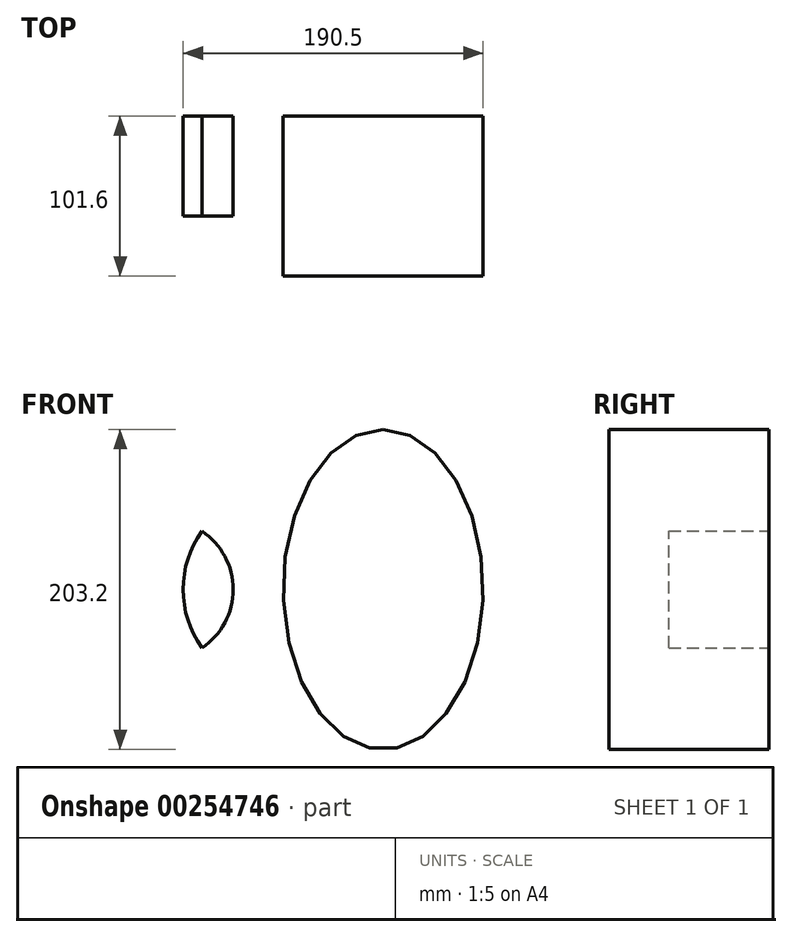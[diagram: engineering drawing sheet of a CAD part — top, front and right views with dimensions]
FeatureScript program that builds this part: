
annotation { "Feature Type Name" : "Feature", "Feature Type Description" : "" }
export const myFeature = defineFeature(function(context is Context, id is Id, definition is map)
    precondition{}
    {
        {
            var Q0;
            Q0=qCreatedBy(makeId("Front.planeOp"),FACE);
            var sketch = newSketch(context, id + "F0", { "sketchPlane" : qUnion([Q0])});
            skLineSegment(sketch, "E0", {"start": v(0, 0) * mm, "end": v(-76.2, 0) * mm});
            skCircle(sketch, "E1", {"center": v(-76.2, 0) * mm, "radius": 44.45 * mm});
            skLineSegment(sketch, "E2", {"start": v(-31.75, 0) * mm, "end": v(-63.5, 0) * mm});
            skCircle(sketch, "E3", {"center": v(0, 0) * mm, "radius": 63.5 * mm});
            skLineSegment(sketch, "E4", {"start": v(63.5, 0) * mm, "end": v(63.5, 101.6) * mm});
            skEllipse(sketch, "E5", {"center": v(63.5, 0) * mm, "majorRadius": 101.6 * mm, "minorRadius": 63.5 * mm, "majorAxis": v(0, 1)});
            skSolve(sketch);
        }
        {
            var Q0;
            {var subQ0=sQuery(id+"F0.wireOp",EDGE,"E3");var subQ1=sQuery(id+"F0.wireOp",EDGE,"E1");var subQ2=makeQuery(id+"F0.imprint","INTERSECT",VERTEX,{"disambiguationData":[OD(0.0)],"derivedFrom":[subQ1,subQ0]});Q0=makeQuery(id+"F0.imprint","IMPRINT",FACE,{"disambiguationData":[TD([[makeQuery(id+"F0.imprint","IMPRINT",EDGE,{"disambiguationData":[TD([[subQ2,-1.0]])],"derivedFrom":subQ1}),1.0]])]});}
            extrude(context, id + "F1", {"entities" : qUnion([Q0]), "depth" : 25.4 * mm});
        }
        {
            var Q0;
            {var subQ3=sQuery(id+"F0.wireOp",EDGE,"E1");var subQ5=sQuery(id+"F0.wireOp",EDGE,"E3");var subQ6=makeQuery(id+"F0.imprint","INTERSECT",VERTEX,{"disambiguationData":[OD(0.0)],"derivedFrom":[subQ3,subQ5]});Q0=makeQuery(id+"F0.imprint","IMPRINT",FACE,{"disambiguationData":[TD([[makeQuery(id+"F0.imprint","IMPRINT",EDGE,{"disambiguationData":[TD([[subQ6,1.0]])],"derivedFrom":subQ5}),1.0]])]});}
            var Q1;
            {var subQ0=sQuery(id+"F0.wireOp",EDGE,"E2");Q1=makeQuery(id+"F0.imprint","IMPRINT",FACE,{"disambiguationData":[TD([[makeQuery(id+"F0.imprint","IMPRINT",EDGE,{"derivedFrom":subQ0}),-1.0]])]});}
            var Q2;
            {var subQ0=sQuery(id+"F0.wireOp",EDGE,"E2");Q2=makeQuery(id+"F0.imprint","IMPRINT",FACE,{"disambiguationData":[TD([[makeQuery(id+"F0.imprint","IMPRINT",EDGE,{"derivedFrom":subQ0}),1.0]])]});}
            var Q3;
            {var subQ3=sQuery(id+"F0.wireOp",EDGE,"E1");var subQ5=sQuery(id+"F0.wireOp",EDGE,"E3");var subQ6=makeQuery(id+"F0.imprint","INTERSECT",VERTEX,{"disambiguationData":[OD(1.0)],"derivedFrom":[subQ3,subQ5]});Q3=makeQuery(id+"F0.imprint","IMPRINT",FACE,{"disambiguationData":[TD([[makeQuery(id+"F0.imprint","IMPRINT",EDGE,{"disambiguationData":[TD([[subQ6,-1.0]])],"derivedFrom":subQ5}),1.0]])]});}
            extrude(context, id + "F2", {"entities" : qUnion([Q0, Q1, Q2, Q3]), "operationType" : NewBodyOperationType.ADD, "depth" : 63.5 * mm});
        }
        {
            var Q0;
            {var subQ0=sQuery(id+"F0.wireOp",EDGE,"E4");Q0=makeQuery(id+"F0.imprint","IMPRINT",FACE,{"disambiguationData":[TD([[makeQuery(id+"F0.imprint","IMPRINT",EDGE,{"derivedFrom":subQ0}),1.0]])]});}
            var Q1;
            {var subQ0=sQuery(id+"F0.wireOp",EDGE,"E4");Q1=makeQuery(id+"F0.imprint","IMPRINT",FACE,{"disambiguationData":[TD([[makeQuery(id+"F0.imprint","IMPRINT",EDGE,{"derivedFrom":subQ0}),-1.0]])]});}
            var Q2;
            {var subQ0=sQuery(id+"F0.wireOp",EDGE,"E3");var subQ1=makeQuery(id+"F0.imprint","INTERSECT",VERTEX,{"derivedFrom":[subQ0,sQuery(id+"F0.wireOp",EDGE,"E4")]});Q2=makeQuery(id+"F0.imprint","IMPRINT",FACE,{"disambiguationData":[TD([[makeQuery(id+"F0.imprint","IMPRINT",EDGE,{"disambiguationData":[TD([[subQ1,-1.0]])],"derivedFrom":subQ0}),1.0]])]});}
            extrude(context, id + "F3", {"entities" : qUnion([Q0, Q1, Q2]), "operationType" : NewBodyOperationType.ADD, "depth" : 101.6 * mm});
        }
    });
